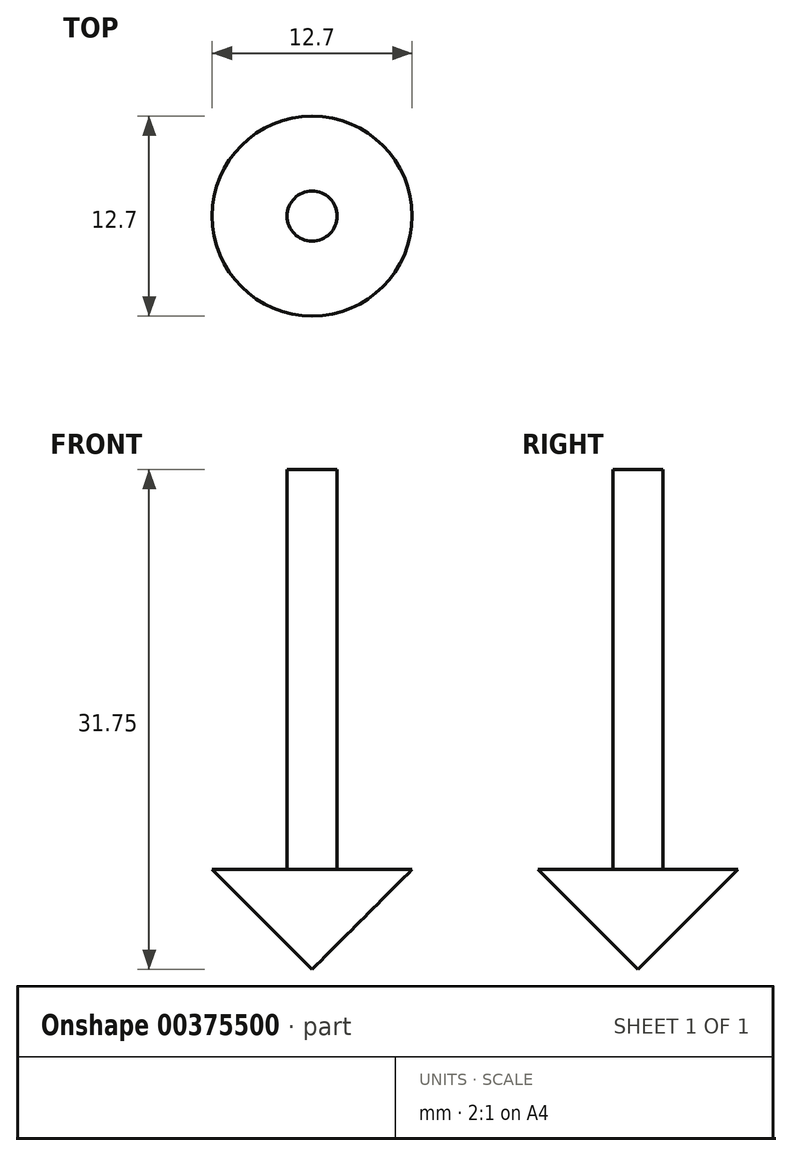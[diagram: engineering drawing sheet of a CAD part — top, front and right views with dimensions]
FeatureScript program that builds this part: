
annotation { "Feature Type Name" : "Feature", "Feature Type Description" : "" }
export const myFeature = defineFeature(function(context is Context, id is Id, definition is map)
    precondition{}
    {
        {
            var Q0;
            Q0=qCreatedBy(makeId("Right.planeOp"),FACE);
            var sketch = newSketch(context, id + "F0", { "sketchPlane" : qUnion([Q0])});
            skLineSegment(sketch, "E0", {"start": v(6.35, 2) * mm, "end": v(6.35, -4.35) * mm});
            skLineSegment(sketch, "E1", {"start": v(6.35, 2) * mm, "end": v(0, 2) * mm});
            skLineSegment(sketch, "E2", {"start": v(6.35, -4.35) * mm, "end": v(0, 2) * mm});
            skSolve(sketch);
        }
        {
            var Q0;
            Q0 = qSketchRegion(id + "F0", true);
            var Q1;
            Q1=sQuery(id+"F0.wireOp",EDGE,"E0");
            revolve(context, id + "F1", {"entities" : qUnion([Q0]), "axis" : qUnion([Q1]), "revolveType" : RevolveType.FULL});
        }
        {
            var Q0;
            Q0=makeQuery(id+"F1.opRevolve","SWEPT_FACE",FACE,{"disambiguationData":[OSD([sQuery(id+"F0.wireOp",EDGE,"E1")])]});
            var sketch = newSketch(context, id + "F2", { "sketchPlane" : qUnion([Q0])});
            skCircle(sketch, "E3", {"center": v(0, 6.35) * mm, "radius": 1.59 * mm});
            skSolve(sketch);
        }
        {
            var Q0;
            Q0 = qSketchRegion(id + "F2", true);
            extrude(context, id + "F3", {"entities" : qUnion([Q0]), "operationType" : NewBodyOperationType.ADD, "depth" : 25.4 * mm});
        }
    });
